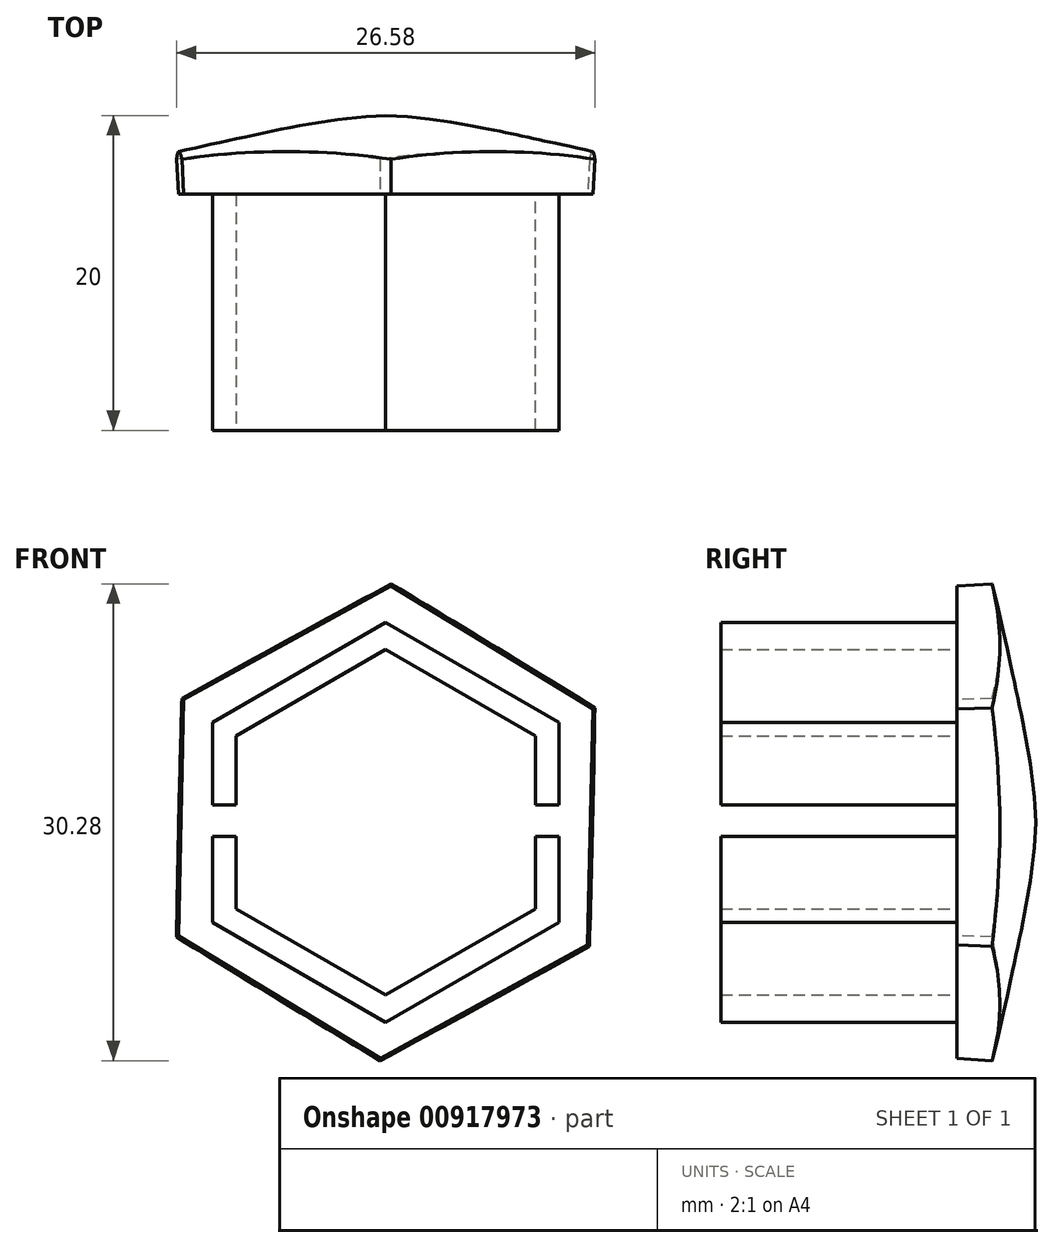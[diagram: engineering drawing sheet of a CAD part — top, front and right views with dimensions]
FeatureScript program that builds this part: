
annotation { "Feature Type Name" : "Feature", "Feature Type Description" : "" }
export const myFeature = defineFeature(function(context is Context, id is Id, definition is map)
    precondition{}
    {
        {
            var Q0;
            Q0=qCreatedBy(makeId("Front.planeOp"),FACE);
            var sketch = newSketch(context, id + "F0", { "sketchPlane" : qUnion([Q0])});
            skCircle(sketch, "E0.cCircle", {"center": v(0, 0) * mm, "radius": 12.7 * mm, "construction": true});
            skLineSegment(sketch, "E0.0", {"start": v(0, -12.7) * mm, "end": v(-11, -6.35) * mm});
            skLineSegment(sketch, "E0.1", {"start": v(-11, -6.35) * mm, "end": v(-11, 6.35) * mm});
            skLineSegment(sketch, "E0.2", {"start": v(-11, 6.35) * mm, "end": v(0, 12.7) * mm});
            skLineSegment(sketch, "E0.3", {"start": v(0, 12.7) * mm, "end": v(11, 6.35) * mm});
            skLineSegment(sketch, "E0.4", {"start": v(11, 6.35) * mm, "end": v(11, -6.35) * mm});
            skLineSegment(sketch, "E0.5", {"start": v(11, -6.35) * mm, "end": v(0, -12.7) * mm});
            skSolve(sketch);
        }
        {
            var Q0;
            Q0=qSketchRegion(id+"F0",true);
            extrude(context, id + "F1", {"entities" : qUnion([Q0]), "depth" : 15 * mm, "offsetDistance" : 25 * mm});
        }
        {
            var Q0;
            Q0=makeQuery(id+"F1.opExtrude","CAP_FACE",FACE,{"disambiguationData":[OSD([sQuery(id+"F0.wireOp",EDGE,"E0.0"),sQuery(id+"F0.wireOp",EDGE,"E0.1"),sQuery(id+"F0.wireOp",EDGE,"E0.2"),sQuery(id+"F0.wireOp",EDGE,"E0.3"),sQuery(id+"F0.wireOp",EDGE,"E0.4"),sQuery(id+"F0.wireOp",EDGE,"E0.5")])],"isStart":false});
            shell(context, id + "F2", {"entities" : qUnion([Q0]), "thickness" : 1.5 * mm});
        }
        {
            var Q0;
            Q0=qCreatedBy(makeId("Top.planeOp"),FACE);
            var sketch = newSketch(context, id + "F3", { "sketchPlane" : qUnion([Q0])});
            skLineSegment(sketch, "E1", {"start": v(0, 0) * mm, "end": v(-16, 0) * mm});
            skLineSegment(sketch, "E2", {"start": v(-16, 0) * mm, "end": v(-16, 2) * mm});
            skFitSpline(sketch, "E3", {"points": [v(-16, 2) * mm, v(-9.06, 3.62) * mm, v(0, 5) * mm], "startDerivative": vector(14.24, 3.9) * mm, "endDerivative": vector(17.69, 0.53) * mm});
            skLineSegment(sketch, "E4", {"start": v(0, 5) * mm, "end": v(0, 0) * mm});
            skSolve(sketch);
        }
        {
            var Q0;
            Q0=makeQuery(id+"F3.imprint","IMPRINT",FACE,{"disambiguationData":[TD([[makeQuery(id+"F3.imprint","IMPRINT",EDGE,{"derivedFrom":sQuery(id+"F3.wireOp",EDGE,"E1")}),-1.0]])]});
            var Q1;
            Q1=sQuery(id+"F3.wireOp",EDGE,"E4");
            revolve(context, id + "F4", {"operationType" : NewBodyOperationType.ADD, "surfaceOperationType" : NewSurfaceOperationType.NEW, "entities" : qUnion([Q0]), "axis" : qUnion([Q1]), "revolveType" : RevolveType.FULL});
        }
        {
            var Q0;
            Q0=qCreatedBy(makeId("Front.planeOp"),FACE);
            var sketch = newSketch(context, id + "F5", { "sketchPlane" : qUnion([Q0])});
            skCircle(sketch, "E5.cCircle", {"center": v(0, 0) * mm, "radius": 15.01 * mm, "construction": true});
            skLineSegment(sketch, "E5.0", {"start": v(12.83, -7.8) * mm, "end": v(-0.34, -15) * mm});
            skLineSegment(sketch, "E5.1", {"start": v(-0.34, -15) * mm, "end": v(-13.17, -7.2) * mm});
            skLineSegment(sketch, "E5.2", {"start": v(-13.17, -7.2) * mm, "end": v(-12.83, 7.8) * mm});
            skLineSegment(sketch, "E5.3", {"start": v(-12.83, 7.8) * mm, "end": v(0.34, 15) * mm});
            skLineSegment(sketch, "E5.4", {"start": v(0.34, 15) * mm, "end": v(13.17, 7.2) * mm});
            skLineSegment(sketch, "E5.5", {"start": v(13.17, 7.2) * mm, "end": v(12.83, -7.8) * mm});
            skSolve(sketch);
        }
        {
            var Q0;
            Q0=makeQuery(id+"F5.imprint","IMPRINT",FACE,{"disambiguationData":[TD([[makeQuery(id+"F5.imprint","IMPRINT",EDGE,{"derivedFrom":sQuery(id+"F5.wireOp",EDGE,"E5.0")}),-1.0]])]});
            extrude(context, id + "F6", {"entities" : qUnion([Q0]), "operationType" : NewBodyOperationType.INTERSECT, "endBound" : BoundingType.THROUGH_ALL, "oppositeDirection" : true, "depth" : 13.44 * mm, "offsetDistance" : 25 * mm, "hasDraft" : true, "draftAngle" : 3 * degree, "hasSecondDirection" : true, "secondDirectionOppositeDirection" : false, "secondDirectionDepth" : 18.5 * mm});
        }
        {
            var Q0;
            Q0=qCreatedBy(makeId("Front.planeOp"),FACE);
            var sketch = newSketch(context, id + "F7", { "sketchPlane" : qUnion([Q0])});
            skLineSegment(sketch, "E6.bottom", {"start": v(12.11, -0.89) * mm, "end": v(-12.2, -0.89) * mm});
            skLineSegment(sketch, "E6.top", {"start": v(12.11, 1.11) * mm, "end": v(-12.2, 1.11) * mm});
            skLineSegment(sketch, "E6.left", {"start": v(12.11, -0.89) * mm, "end": v(12.11, 1.11) * mm});
            skLineSegment(sketch, "E6.right", {"start": v(-12.2, -0.89) * mm, "end": v(-12.2, 1.11) * mm});
            skSolve(sketch);
        }
        {
            var Q0;
            Q0=makeQuery(id+"F7.imprint","IMPRINT",FACE,{"disambiguationData":[TD([[makeQuery(id+"F7.imprint","IMPRINT",EDGE,{"derivedFrom":sQuery(id+"F7.wireOp",EDGE,"E6.bottom")}),-1.0]])]});
            extrude(context, id + "F8", {"entities" : qUnion([Q0]), "operationType" : NewBodyOperationType.REMOVE, "depth" : 20 * mm, "offsetDistance" : 25 * mm});
        }
        {
            var Q0;
            {var subQ0=sQuery(id+"F0.wireOp",EDGE,"E0.4");var subQ1=sQuery(id+"F0.wireOp",EDGE,"E0.3");var subQ2=sQuery(id+"F0.wireOp",EDGE,"E0.2");var subQ3=sQuery(id+"F0.wireOp",EDGE,"E0.1");Q0=makeQuery(id+"F8.boolean.opBoolean","SPLIT",FACE,{"disambiguationData":[TD([makeQuery(id+"F2.opShell","OFFSET_FACE",FACE,{"disambiguationData":[OSD([subQ2])]})])],"derivedFrom":makeQuery(id+"F2.opShell","OFFSET_FACE",FACE,{"disambiguationData":[OSD([sQuery(id+"F0.wireOp",EDGE,"E0.0"),subQ3,subQ2,subQ1,subQ0,sQuery(id+"F0.wireOp",EDGE,"E0.5")])]})});}
            extrude(context, id + "F9", {"entities" : qUnion([Q0]), "operationType" : NewBodyOperationType.REMOVE, "oppositeDirection" : true, "depth" : 1.5 * mm, "offsetDistance" : 25 * mm});
        }
        {
            var Q0;
            {var subQ0=sQuery(id+"F0.wireOp",EDGE,"E0.5");var subQ1=sQuery(id+"F0.wireOp",EDGE,"E0.1");var subQ2=sQuery(id+"F0.wireOp",EDGE,"E0.4");var subQ3=sQuery(id+"F0.wireOp",EDGE,"E0.0");Q0=makeQuery(id+"F8.boolean.opBoolean","SPLIT",FACE,{"disambiguationData":[TD([makeQuery(id+"F2.opShell","OFFSET_FACE",FACE,{"disambiguationData":[OSD([subQ3])]})])],"derivedFrom":makeQuery(id+"F2.opShell","OFFSET_FACE",FACE,{"disambiguationData":[OSD([subQ3,subQ1,sQuery(id+"F0.wireOp",EDGE,"E0.2"),sQuery(id+"F0.wireOp",EDGE,"E0.3"),subQ2,subQ0])]})});}
            extrude(context, id + "F10", {"entities" : qUnion([Q0]), "operationType" : NewBodyOperationType.REMOVE, "oppositeDirection" : true, "depth" : 1.5 * mm, "offsetDistance" : 25 * mm});
        }
    });
